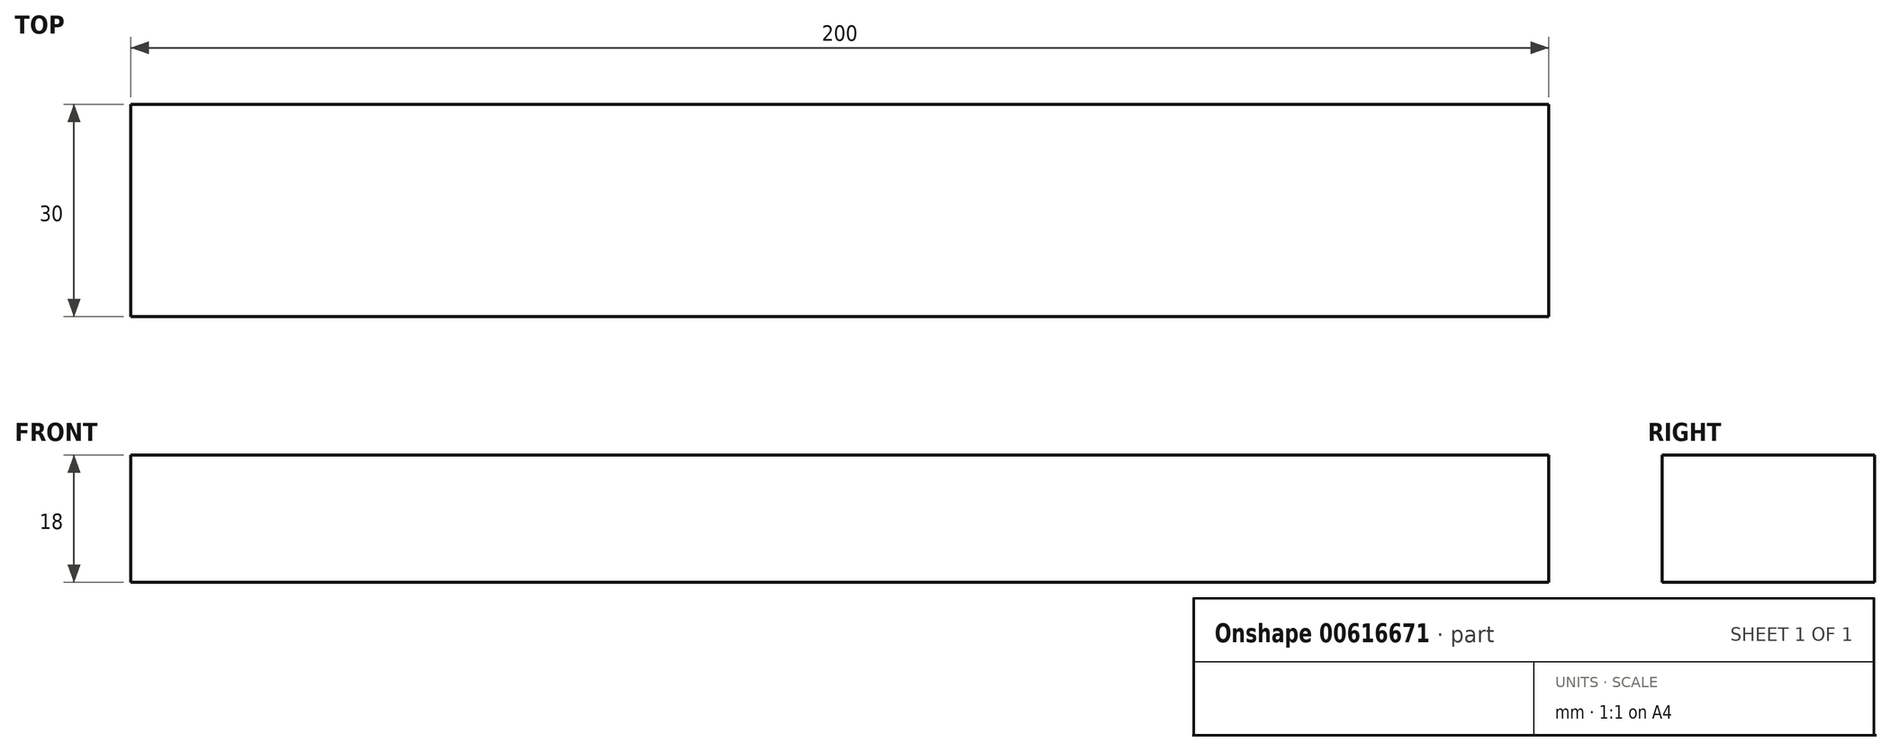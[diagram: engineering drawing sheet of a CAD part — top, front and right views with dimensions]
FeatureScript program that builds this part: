
annotation { "Feature Type Name" : "Feature", "Feature Type Description" : "" }
export const myFeature = defineFeature(function(context is Context, id is Id, definition is map)
    precondition{}
    {
        {
            var Q0;
            Q0=qCreatedBy(makeId("Top.planeOp"),FACE);
            var sketch = newSketch(context, id + "F0", { "sketchPlane" : qUnion([Q0])});
            skLineSegment(sketch, "E0.bottom", {"start": v(0, 0) * mm, "end": v(200, 0) * mm});
            skLineSegment(sketch, "E0.top", {"start": v(0, 30) * mm, "end": v(200, 30) * mm});
            skLineSegment(sketch, "E0.left", {"start": v(0, 0) * mm, "end": v(0, 30) * mm});
            skLineSegment(sketch, "E0.right", {"start": v(200, 0) * mm, "end": v(200, 30) * mm});
            skSolve(sketch);
        }
        {
            var Q0;
            Q0=makeQuery(id+"F0.imprint","IMPRINT",FACE,{"disambiguationData":[TD([[makeQuery(id+"F0.imprint","IMPRINT",EDGE,{"derivedFrom":sQuery(id+"F0.wireOp",EDGE,"E0.bottom")}),1.0]])]});
            extrude(context, id + "F1", {"entities" : qUnion([Q0]), "depth" : 18 * mm, "offsetDistance" : 25 * mm});
        }
    });
